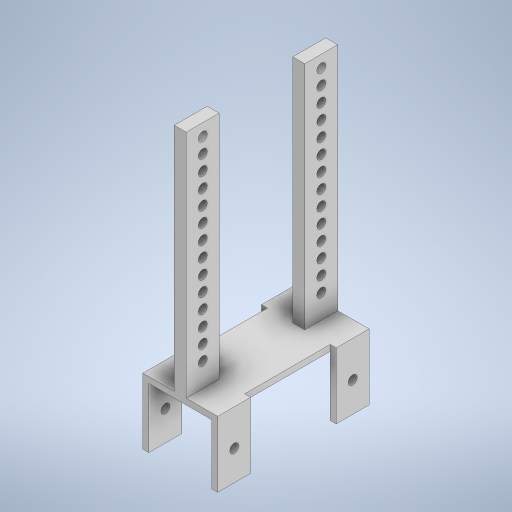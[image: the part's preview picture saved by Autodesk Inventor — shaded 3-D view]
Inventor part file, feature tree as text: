
AUTODESK INVENTOR PART (.ipt)
format: ipt  version: 2024 (Build 280153000, 153)  size: 389,632 bytes
history: native  units: mm
features: extrude x6, sketch x5, projected_geometry x3
ambient origin geometry x8: Origin, YZ Plane, XZ Plane, XY Plane, X Axis, Y Axis, Z Axis, Center Point
bodies: Body1 (feature_tree), Body2 (feature_tree)
feature tree (14):
  extrude  "돌출3"  Depth=11.0mm
  sketch  "스케치5"
  extrude  "돌출4"  Depth=4.0mm
  extrude  "돌출5"  Depth=77.0mm TaperAngle=0.0deg
  extrude  "돌출6"  Depth=21.0mm
  extrude  "돌출7"  Depth=11.0mm
  extrude  "돌출8"  Depth=2.0mm
  sketch  "스케치4"
  sketch  "스케치6"
  projected_geometry  "투영된 루프1"
  sketch  "스케치7"
  projected_geometry  "투영된 루프2"
  sketch  "스케치9"
  projected_geometry  "투영된 루프3"
